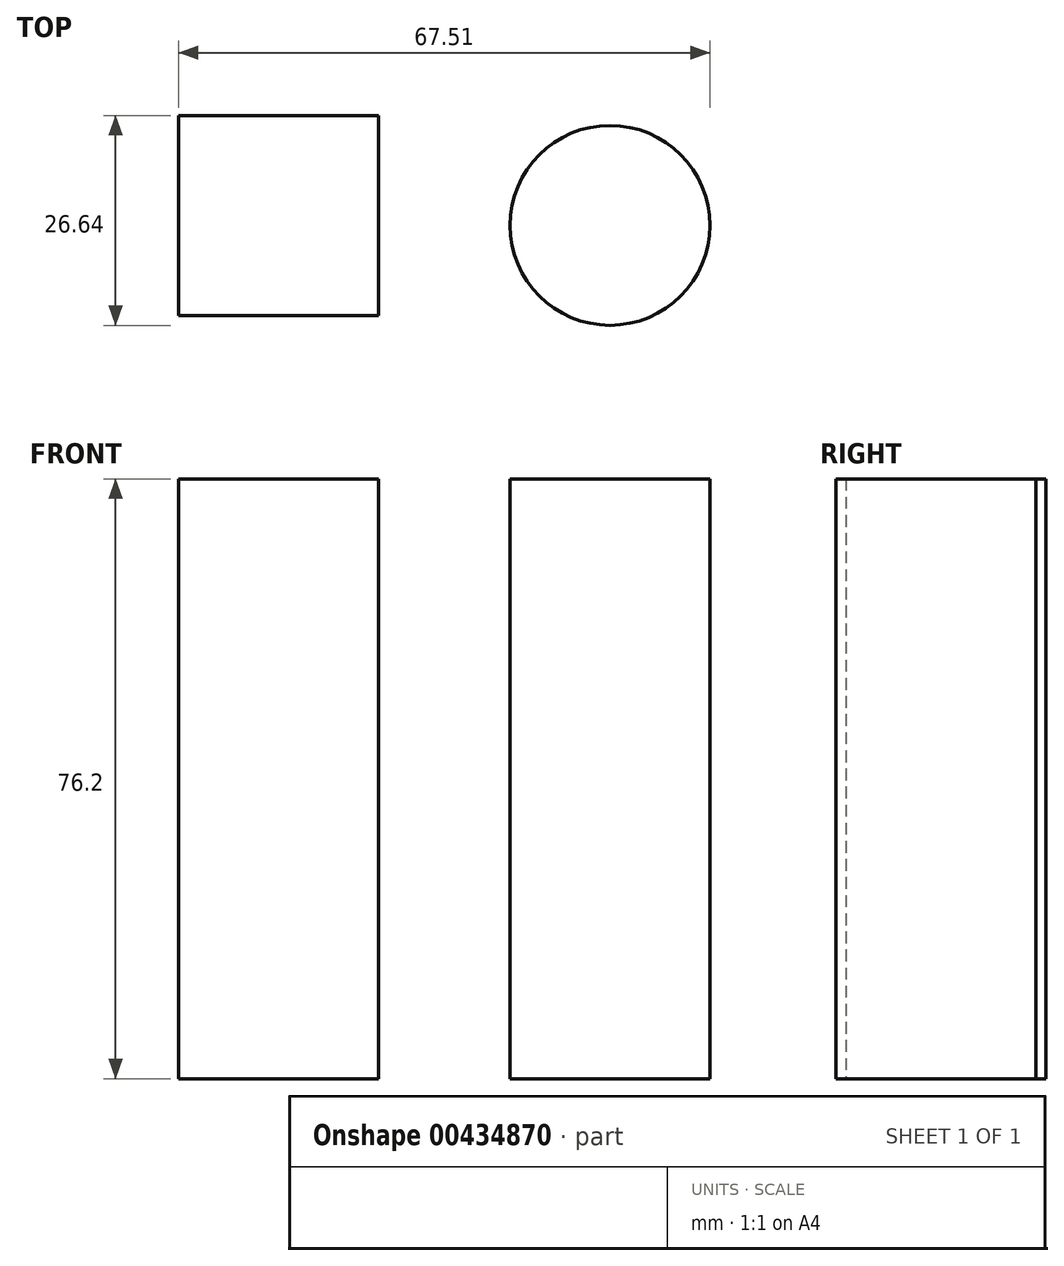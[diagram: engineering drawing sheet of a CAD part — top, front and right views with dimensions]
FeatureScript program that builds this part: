
annotation { "Feature Type Name" : "Feature", "Feature Type Description" : "" }
export const myFeature = defineFeature(function(context is Context, id is Id, definition is map)
    precondition{}
    {
        {
            var Q0;
            Q0=qCreatedBy(makeId("Top.planeOp"),FACE);
            var sketch = newSketch(context, id + "F0", { "sketchPlane" : qUnion([Q0])});
            skLineSegment(sketch, "E0.bottom", {"start": v(-59.77, 0) * mm, "end": v(-34.37, 0) * mm});
            skLineSegment(sketch, "E0.top", {"start": v(-59.77, -25.4) * mm, "end": v(-34.37, -25.4) * mm});
            skLineSegment(sketch, "E0.left", {"start": v(-59.77, 0) * mm, "end": v(-59.77, -25.4) * mm});
            skLineSegment(sketch, "E0.right", {"start": v(-34.37, 0) * mm, "end": v(-34.37, -25.4) * mm});
            skCircle(sketch, "E1", {"center": v(-4.96, -13.94) * mm, "radius": 12.7 * mm});
            skSolve(sketch);
        }
        {
            var Q0;
            Q0 = qSketchRegion(id + "F0", true);
            extrude(context, id + "F1", {"entities" : qUnion([Q0]), "depth" : 76.2 * mm});
        }
    });
